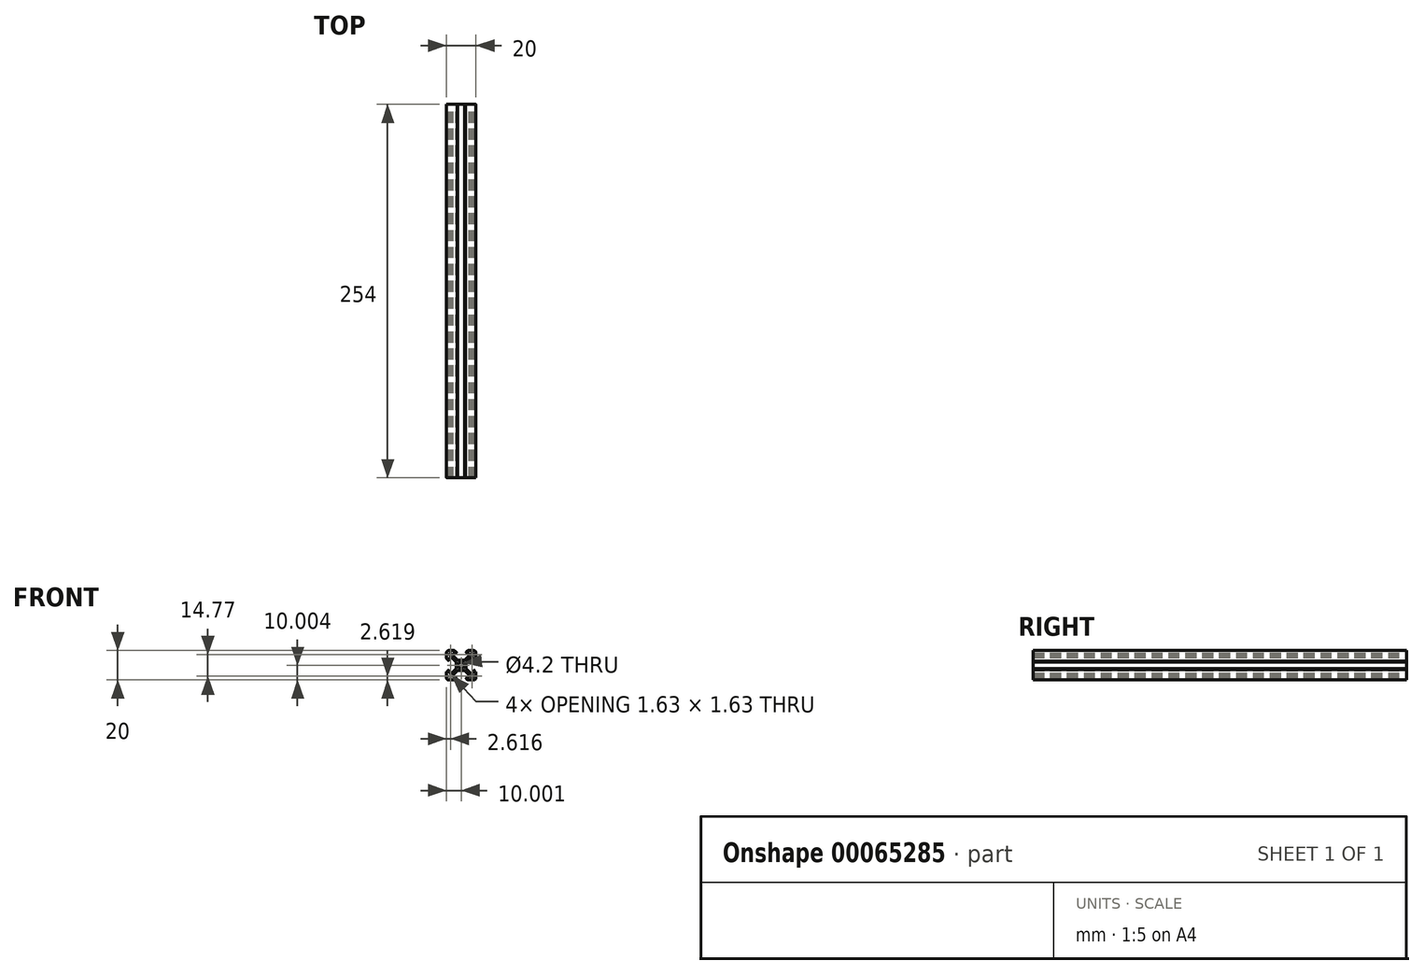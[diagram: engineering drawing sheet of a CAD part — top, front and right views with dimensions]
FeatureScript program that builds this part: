
annotation { "Feature Type Name" : "Feature", "Feature Type Description" : "" }
export const myFeature = defineFeature(function(context is Context, id is Id, definition is map)
    precondition{}
    {
        {
            var Q0;
            Q0=qCreatedBy(makeId("Front.planeOp"),FACE);
            var sketch = newSketch(context, id + "F0", { "sketchPlane" : qUnion([Q0])});
            skLineSegment(sketch, "E0.MirrorCS", {"start": v(-126.2, 11.58) * mm, "end": v(-123.04, 8.42) * mm});
            skPoint(sketch, "E1.endSnap0", {"position": v(-129.6, 17.32) * mm});
            skLineSegment(sketch, "E2", {"start": v(-129.6, 13.92) * mm, "end": v(-122.85, 13.92) * mm, "construction": true});
            skLineSegment(sketch, "E3.MirrorCS", {"start": v(-126.7, 5.72) * mm, "end": v(-124.1, 5.72) * mm});
            skLineSegment(sketch, "E4.MirrorCS", {"start": v(-124.1, 7.36) * mm, "end": v(-127.26, 10.52) * mm});
            skLineSegment(sketch, "E5.MirrorCS", {"start": v(-131.94, 10.52) * mm, "end": v(-127.26, 10.52) * mm});
            skLineSegment(sketch, "E6.MirrorCS", {"start": v(-137.8, 8.42) * mm, "end": v(-137.8, 11.03) * mm});
            skLineSegment(sketch, "E7.0", {"start": v(-133, 16.26) * mm, "end": v(-136.16, 19.42) * mm});
            skArc(sketch, "E8.MirrorCS", {"start": v(-119.6, 22.42) * mm, "mid": v(-120.04, 23.48) * mm, "end": v(-121.1, 23.92) * mm});
            skLineSegment(sketch, "E9.MirrorCS", {"start": v(-139.6, 9.02) * mm, "end": v(-139.6, 5.42) * mm});
            skLineSegment(sketch, "E10.MirrorCS", {"start": v(-125.25, 23.7) * mm, "end": v(-126.7, 22.23) * mm});
            skLineSegment(sketch, "E11.1", {"start": v(-139.6, 18.83) * mm, "end": v(-139.6, 22.42) * mm});
            skLineSegment(sketch, "E12.0", {"start": v(-132.49, 22.12) * mm, "end": v(-135.1, 22.12) * mm});
            skLineSegment(sketch, "E13.MirrorCS", {"start": v(-126.2, 11.58) * mm, "end": v(-126.2, 16.26) * mm});
            skLineSegment(sketch, "E14.MirrorCS", {"start": v(-138.1, 3.92) * mm, "end": v(-134.5, 3.92) * mm});
            skLineSegment(sketch, "E15.MirrorCS", {"start": v(-119.6, 18.83) * mm, "end": v(-119.6, 22.42) * mm});
            skLineSegment(sketch, "E16.0", {"start": v(-138.1, 23.92) * mm, "end": v(-134.5, 23.92) * mm});
            skArc(sketch, "E17.MirrorCS", {"start": v(-139.6, 5.42) * mm, "mid": v(-139.16, 4.36) * mm, "end": v(-138.1, 3.92) * mm});
            skLineSegment(sketch, "E18.0", {"start": v(-135.1, 20.48) * mm, "end": v(-131.94, 17.32) * mm});
            skLineSegment(sketch, "E19.MirrorCS", {"start": v(-124.1, 20.48) * mm, "end": v(-127.26, 17.32) * mm});
            skLineSegment(sketch, "E20.0", {"start": v(-131.94, 17.32) * mm, "end": v(-127.26, 17.32) * mm});
            skCircle(sketch, "E21.0", {"center": v(-129.6, 13.92) * mm, "radius": 2.1 * mm});
            skLineSegment(sketch, "E22.MirrorCS", {"start": v(-133, 11.58) * mm, "end": v(-136.16, 8.42) * mm});
            skLineSegment(sketch, "E23.MirrorCS", {"start": v(-121.4, 8.42) * mm, "end": v(-121.4, 11.03) * mm});
            skLineSegment(sketch, "E24.0", {"start": v(-137.8, 19.42) * mm, "end": v(-137.8, 16.81) * mm});
            skLineSegment(sketch, "E25.MirrorCS", {"start": v(-121.4, 19.42) * mm, "end": v(-121.4, 16.81) * mm});
            skLineSegment(sketch, "E26.MirrorCS", {"start": v(-126.2, 16.26) * mm, "end": v(-123.04, 19.42) * mm});
            skLineSegment(sketch, "E27.0", {"start": v(-137.9, 16.81) * mm, "end": v(-139.37, 18.27) * mm});
            skLineSegment(sketch, "E28.MirrorCS", {"start": v(-132.49, 5.72) * mm, "end": v(-135.1, 5.72) * mm});
            skArc(sketch, "E29.MirrorCS", {"start": v(-119.6, 5.42) * mm, "mid": v(-120.04, 4.36) * mm, "end": v(-121.1, 3.92) * mm});
            skLineSegment(sketch, "E30.MirrorCS", {"start": v(-126.7, 22.12) * mm, "end": v(-124.1, 22.12) * mm});
            skLineSegment(sketch, "E31.MirrorCS", {"start": v(-135.1, 7.36) * mm, "end": v(-131.94, 10.52) * mm});
            skLineSegment(sketch, "E32.0", {"start": v(-133, 11.58) * mm, "end": v(-133, 16.26) * mm});
            skLineSegment(sketch, "E1", {"start": v(-129.6, 13.92) * mm, "end": v(-129.6, 23.9) * mm, "construction": true});
            skLineSegment(sketch, "E33.MirrorCS", {"start": v(-121.1, 23.92) * mm, "end": v(-124.7, 23.92) * mm});
            skArc(sketch, "E11.0", {"start": v(-139.6, 22.42) * mm, "mid": v(-139.16, 23.48) * mm, "end": v(-138.1, 23.92) * mm});
            skLineSegment(sketch, "E34.MirrorCS", {"start": v(-121.1, 3.92) * mm, "end": v(-124.7, 3.92) * mm});
            skLineSegment(sketch, "E35.MirrorCS", {"start": v(-119.6, 9.02) * mm, "end": v(-119.6, 5.42) * mm});
            skLineSegment(sketch, "E36.MirrorCS", {"start": v(-124.1, 5.72) * mm, "end": v(-124.1, 7.36) * mm});
            skLineSegment(sketch, "E37.MirrorCS", {"start": v(-124.1, 22.12) * mm, "end": v(-124.1, 20.48) * mm});
            skLineSegment(sketch, "E38.MirrorCS", {"start": v(-123.04, 8.42) * mm, "end": v(-121.4, 8.42) * mm});
            skLineSegment(sketch, "E39.0", {"start": v(-136.16, 19.42) * mm, "end": v(-137.8, 19.42) * mm});
            skLineSegment(sketch, "E40.MirrorCS", {"start": v(-121.4, 7.35) * mm, "end": v(-121.4, 5.72) * mm});
            skLineSegment(sketch, "E41.MirrorCS", {"start": v(-123.03, 22.12) * mm, "end": v(-123.03, 21.58) * mm});
            skLineSegment(sketch, "E42.0", {"start": v(-133.95, 23.7) * mm, "end": v(-132.49, 22.23) * mm});
            skArc(sketch, "E43.MirrorCS", {"start": v(-124.7, 23.92) * mm, "mid": v(-125, 23.86) * mm, "end": v(-125.25, 23.7) * mm});
            skLineSegment(sketch, "E44.MirrorCS", {"start": v(-137.26, 7.35) * mm, "end": v(-137.8, 7.35) * mm});
            skLineSegment(sketch, "E45.MirrorCS", {"start": v(-136.16, 8.42) * mm, "end": v(-137.8, 8.42) * mm});
            skLineSegment(sketch, "E46.0", {"start": v(-136.17, 21.58) * mm, "end": v(-137.26, 20.5) * mm});
            skLineSegment(sketch, "E47.MirrorCS", {"start": v(-121.4, 22.12) * mm, "end": v(-123.03, 22.12) * mm});
            skArc(sketch, "E48.MirrorCS", {"start": v(-119.83, 18.27) * mm, "mid": v(-119.66, 18.53) * mm, "end": v(-119.6, 18.83) * mm});
            skArc(sketch, "E49.0", {"start": v(-134.5, 23.92) * mm, "mid": v(-134.2, 23.86) * mm, "end": v(-133.95, 23.7) * mm});
            skArc(sketch, "E50.MirrorCS", {"start": v(-119.83, 9.57) * mm, "mid": v(-119.66, 9.32) * mm, "end": v(-119.6, 9.02) * mm});
            skLineSegment(sketch, "E51.MirrorCS", {"start": v(-133.95, 4.15) * mm, "end": v(-132.49, 5.61) * mm});
            skLineSegment(sketch, "E52.MirrorCS", {"start": v(-123.04, 19.42) * mm, "end": v(-121.4, 19.42) * mm});
            skLineSegment(sketch, "E53.MirrorCS", {"start": v(-136.17, 6.26) * mm, "end": v(-137.26, 7.35) * mm});
            skLineSegment(sketch, "E54.MirrorCS", {"start": v(-121.94, 7.35) * mm, "end": v(-121.4, 7.35) * mm});
            skLineSegment(sketch, "E55.MirrorCS", {"start": v(-123.03, 5.72) * mm, "end": v(-123.03, 6.26) * mm});
            skLineSegment(sketch, "E56.0", {"start": v(-136.17, 22.12) * mm, "end": v(-136.17, 21.58) * mm});
            skLineSegment(sketch, "E57.MirrorCS", {"start": v(-121.4, 5.72) * mm, "end": v(-123.03, 5.72) * mm});
            skLineSegment(sketch, "E58.0", {"start": v(-137.26, 20.5) * mm, "end": v(-137.8, 20.5) * mm});
            skLineSegment(sketch, "E59", {"start": v(-126.7, 5.72) * mm, "end": v(-126.7, 5.61) * mm});
            skLineSegment(sketch, "E60.MirrorCS", {"start": v(-121.29, 11.03) * mm, "end": v(-119.83, 9.57) * mm});
            skArc(sketch, "E61.MirrorCS", {"start": v(-139.37, 9.57) * mm, "mid": v(-139.54, 9.32) * mm, "end": v(-139.6, 9.02) * mm});
            skLineSegment(sketch, "E62.MirrorCS", {"start": v(-136.17, 5.72) * mm, "end": v(-136.17, 6.26) * mm});
            skLineSegment(sketch, "E63", {"start": v(-132.49, 5.72) * mm, "end": v(-132.49, 5.61) * mm});
            skLineSegment(sketch, "E64.0", {"start": v(-135.1, 22.12) * mm, "end": v(-135.1, 20.48) * mm});
            skLineSegment(sketch, "E65.MirrorCS", {"start": v(-137.9, 11.03) * mm, "end": v(-139.37, 9.57) * mm});
            skLineSegment(sketch, "E66.MirrorCS", {"start": v(-135.1, 5.72) * mm, "end": v(-135.1, 7.36) * mm});
            skArc(sketch, "E67.MirrorCS", {"start": v(-124.7, 3.92) * mm, "mid": v(-125, 3.98) * mm, "end": v(-125.25, 4.15) * mm});
            skArc(sketch, "E68.0", {"start": v(-139.37, 18.27) * mm, "mid": v(-139.54, 18.53) * mm, "end": v(-139.6, 18.83) * mm});
            skArc(sketch, "E69.MirrorCS", {"start": v(-134.5, 3.92) * mm, "mid": v(-134.2, 3.98) * mm, "end": v(-133.95, 4.15) * mm});
            skLineSegment(sketch, "E70.0", {"start": v(-137.8, 20.5) * mm, "end": v(-137.8, 22.12) * mm});
            skLineSegment(sketch, "E71.MirrorCS", {"start": v(-123.03, 6.26) * mm, "end": v(-121.94, 7.35) * mm});
            skLineSegment(sketch, "E72.MirrorCS", {"start": v(-121.94, 20.5) * mm, "end": v(-121.4, 20.5) * mm});
            skLineSegment(sketch, "E73.MirrorCS", {"start": v(-125.25, 4.15) * mm, "end": v(-126.7, 5.61) * mm});
            skLineSegment(sketch, "E74.MirrorCS", {"start": v(-121.4, 20.5) * mm, "end": v(-121.4, 22.12) * mm});
            skLineSegment(sketch, "E75.0", {"start": v(-137.8, 22.12) * mm, "end": v(-136.17, 22.12) * mm});
            skLineSegment(sketch, "E76.MirrorCS", {"start": v(-137.8, 7.35) * mm, "end": v(-137.8, 5.72) * mm});
            skLineSegment(sketch, "E77.MirrorCS", {"start": v(-137.8, 5.72) * mm, "end": v(-136.17, 5.72) * mm});
            skLineSegment(sketch, "E78.MirrorCS", {"start": v(-123.03, 21.58) * mm, "end": v(-121.94, 20.5) * mm});
            skLineSegment(sketch, "E79.MirrorCS", {"start": v(-121.29, 16.81) * mm, "end": v(-119.83, 18.27) * mm});
            skLineSegment(sketch, "E80", {"start": v(-121.29, 11.03) * mm, "end": v(-121.4, 11.03) * mm});
            skLineSegment(sketch, "E81", {"start": v(-137.8, 11.03) * mm, "end": v(-137.9, 11.03) * mm});
            skLineSegment(sketch, "E82", {"start": v(-132.49, 22.23) * mm, "end": v(-132.49, 22.12) * mm});
            skLineSegment(sketch, "E83", {"start": v(-121.4, 16.81) * mm, "end": v(-121.29, 16.81) * mm});
            skLineSegment(sketch, "E84", {"start": v(-126.7, 22.12) * mm, "end": v(-126.7, 22.23) * mm});
            skLineSegment(sketch, "E85", {"start": v(-137.8, 16.81) * mm, "end": v(-137.9, 16.81) * mm});
            skSolve(sketch);
        }
        {
            var Q0;
            Q0 = qSketchRegion(id + "F0", true);
            extrude(context, id + "F1", {"entities" : qUnion([Q0]), "depth" : 254 * mm});
        }
    });
